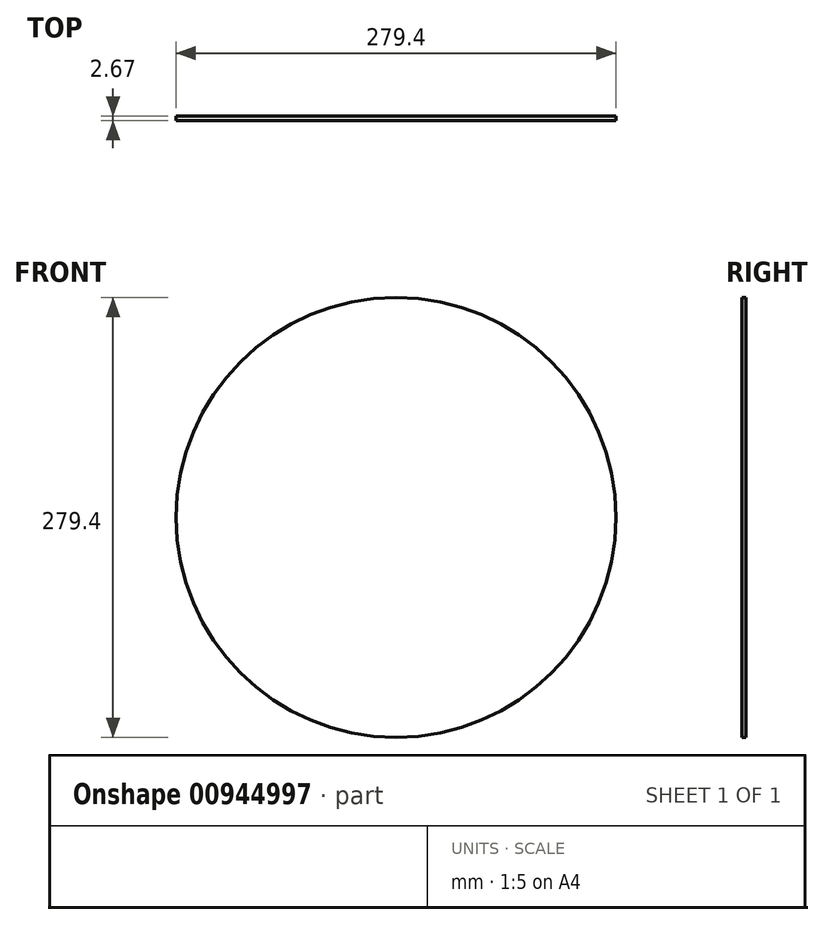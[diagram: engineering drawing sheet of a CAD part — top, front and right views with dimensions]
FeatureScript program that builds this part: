
annotation { "Feature Type Name" : "Feature", "Feature Type Description" : "" }
export const myFeature = defineFeature(function(context is Context, id is Id, definition is map)
    precondition{}
    {
        {
            var Q0;
            Q0=qCreatedBy(makeId("Front.planeOp"),FACE);
            var sketch = newSketch(context, id + "F0", { "sketchPlane" : qUnion([Q0])});
            skCircle(sketch, "E0", {"center": v(0, 0) * mm, "radius": 139.7 * mm});
            skSolve(sketch);
        }
        {
            var Q0;
            Q0 = qSketchRegion(id + "F0", true);
            extrude(context, id + "F1", {"entities" : qUnion([Q0]), "depth" : 2.67 * mm, "offsetDistance" : 25.4 * mm});
        }
    });
